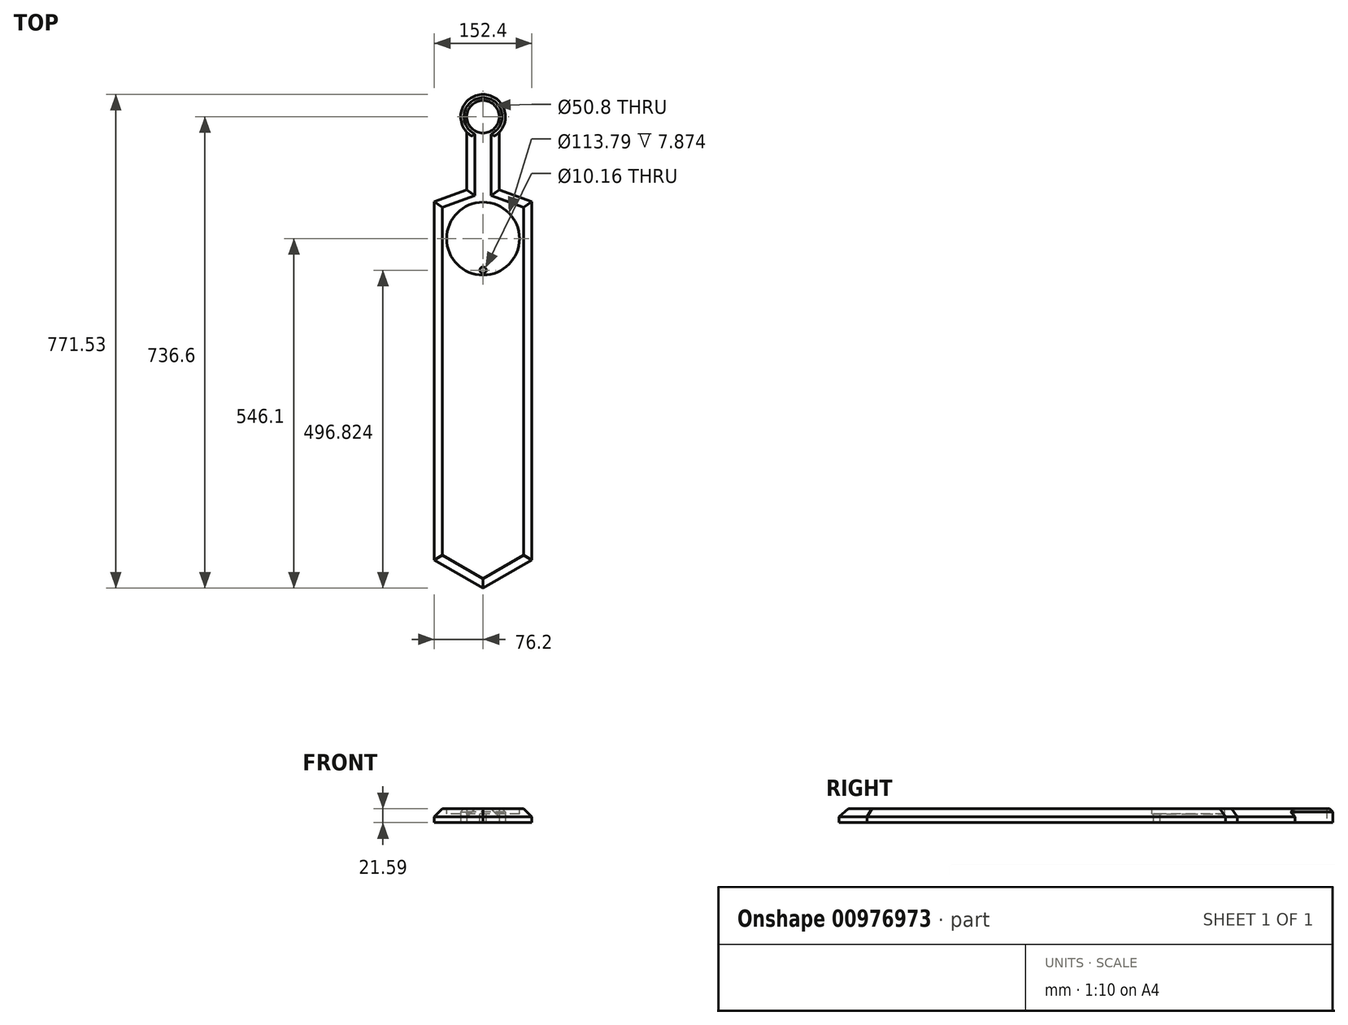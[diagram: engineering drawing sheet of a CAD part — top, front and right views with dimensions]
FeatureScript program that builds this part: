
annotation { "Feature Type Name" : "Feature", "Feature Type Description" : "" }
export const myFeature = defineFeature(function(context is Context, id is Id, definition is map)
    precondition{}
    {
        {
            var Q0;
            Q0=qCreatedBy(makeId("Top.planeOp"),FACE);
            var sketch = newSketch(context, id + "F0", { "sketchPlane" : qUnion([Q0])});
            skCircle(sketch, "E0", {"center": v(0, 0) * mm, "radius": 25.4 * mm});
            skLineSegment(sketch, "E1", {"start": v(-25.4, 0) * mm, "end": v(-25.4, -114.3) * mm});
            skLineSegment(sketch, "E2", {"start": v(-25.4, -114.3) * mm, "end": v(-76.2, -132.79) * mm});
            skLineSegment(sketch, "E3", {"start": v(-76.2, -132.79) * mm, "end": v(-76.2, -692.6) * mm});
            skLineSegment(sketch, "E4", {"start": v(0, -736.6) * mm, "end": v(-76.2, -692.6) * mm});
            skLineSegment(sketch, "E5", {"start": v(0, 0) * mm, "end": v(0, -736.6) * mm, "construction": true});
            skLineSegment(sketch, "E6.MirrorCS", {"start": v(76.2, -132.79) * mm, "end": v(76.2, -692.6) * mm});
            skLineSegment(sketch, "E7.MirrorCS", {"start": v(0, -736.6) * mm, "end": v(76.2, -692.6) * mm});
            skLineSegment(sketch, "E8.MirrorCS", {"start": v(25.4, 0) * mm, "end": v(25.4, -114.3) * mm});
            skLineSegment(sketch, "E9.MirrorCS", {"start": v(25.4, -114.3) * mm, "end": v(76.2, -132.79) * mm});
            skCircle(sketch, "E10", {"center": v(0, 0) * mm, "radius": 34.93 * mm});
            skSolve(sketch);
        }
        {
            var Q0;
            {var subQ0=sQuery(id+"F0.wireOp",EDGE,"E1");Q0=makeQuery(id+"F0.imprint","IMPRINT",FACE,{"disambiguationData":[TD([[makeQuery(id+"F0.imprint","IMPRINT",EDGE,{"derivedFrom":subQ0}),1.0]])]});}
            var Q1;
            {var subQ0=sQuery(id+"F0.wireOp",EDGE,"E0");var subQ1=makeQuery(id+"F0.imprint","INTERSECT",VERTEX,{"derivedFrom":[sQuery(id+"F0.wireOp",EDGE,"E1"),subQ0]});Q1=makeQuery(id+"F0.imprint","IMPRINT",FACE,{"disambiguationData":[TD([[makeQuery(id+"F0.imprint","IMPRINT",EDGE,{"disambiguationData":[TD([[subQ1,-1.0]])],"derivedFrom":subQ0}),-1.0]])]});}
            var Q2;
            {var subQ0=sQuery(id+"F0.wireOp",EDGE,"E0");var subQ1=sQuery(id+"F0.wireOp",EDGE,"E1");var subQ2=makeQuery(id+"F0.imprint","INTERSECT",VERTEX,{"derivedFrom":[subQ1,subQ0]});Q2=makeQuery(id+"F0.imprint","IMPRINT",FACE,{"disambiguationData":[TD([[makeQuery(id+"F0.imprint","IMPRINT",EDGE,{"disambiguationData":[TD([[subQ2,-1.0]])],"derivedFrom":subQ1}),-1.0]])]});}
            var Q3;
            {var subQ0=sQuery(id+"F0.wireOp",EDGE,"E2");Q3=makeQuery(id+"F0.imprint","IMPRINT",FACE,{"disambiguationData":[TD([[makeQuery(id+"F0.imprint","IMPRINT",EDGE,{"derivedFrom":subQ0}),1.0]])]});}
            extrude(context, id + "F1", {"entities" : qUnion([Q0, Q1, Q2, Q3]), "depth" : 21.59 * mm, "offsetDistance" : 25.4 * mm});
        }
        {
            var Q0;
            Q0=makeQuery(id+"F1.opExtrude","CAP_FACE",FACE,{"disambiguationData":[OSD([sQuery(id+"F0.wireOp",EDGE,"E1"),sQuery(id+"F0.wireOp",EDGE,"E2"),sQuery(id+"F0.wireOp",EDGE,"E3"),sQuery(id+"F0.wireOp",EDGE,"E4"),sQuery(id+"F0.wireOp",EDGE,"E6.MirrorCS"),sQuery(id+"F0.wireOp",EDGE,"E7.MirrorCS"),sQuery(id+"F0.wireOp",EDGE,"E8.MirrorCS"),sQuery(id+"F0.wireOp",EDGE,"E9.MirrorCS"),sQuery(id+"F0.wireOp",EDGE,"E10")])],"isStart":false});
            var sketch = newSketch(context, id + "F2", { "sketchPlane" : qUnion([Q0])});
            skCircle(sketch, "E11", {"center": v(0, -190.5) * mm, "radius": 56.9 * mm});
            skSolve(sketch);
        }
        {
            var Q0;
            Q0=makeQuery(id+"F2.imprint","IMPRINT",FACE,{"disambiguationData":[TD([[makeQuery(id+"F2.imprint","IMPRINT",EDGE,{"derivedFrom":sQuery(id+"F2.wireOp",EDGE,"E11")}),1.0]])]});
            extrude(context, id + "F3", {"entities" : qUnion([Q0]), "operationType" : NewBodyOperationType.REMOVE, "oppositeDirection" : true, "depth" : 7.87 * mm, "offsetDistance" : 25.4 * mm});
        }
        {
            var Q0;
            Q0=makeQuery(id+"F3.boolean.opBoolean","COPY",FACE,{"derivedFrom":makeQuery(id+"F3.opExtrude","CAP_FACE",FACE,{"disambiguationData":[OSD([sQuery(id+"F2.wireOp",EDGE,"E11")])],"isStart":false})});
            var sketch = newSketch(context, id + "F4", { "sketchPlane" : qUnion([Q0])});
            skCircle(sketch, "E12", {"center": v(0, -239.78) * mm, "radius": 5.08 * mm});
            skSolve(sketch);
        }
        {
            var Q0;
            Q0=makeQuery(id+"F4.imprint","IMPRINT",FACE,{"disambiguationData":[TD([[makeQuery(id+"F4.imprint","IMPRINT",EDGE,{"derivedFrom":sQuery(id+"F4.wireOp",EDGE,"E12")}),1.0]])]});
            extrude(context, id + "F5", {"entities" : qUnion([Q0]), "operationType" : NewBodyOperationType.REMOVE, "endBound" : BoundingType.THROUGH_ALL, "oppositeDirection" : true, "depth" : 25.4 * mm, "offsetDistance" : 25.4 * mm});
        }
        {
            var Q0;
            Q0=makeQuery(id+"F1.opExtrude","CAP_EDGE",EDGE,{"disambiguationData":[OSD([sQuery(id+"F0.wireOp",EDGE,"E3")])],"isStart":false});
            var Q1;
            Q1=makeQuery(id+"F1.opExtrude","CAP_EDGE",EDGE,{"disambiguationData":[OSD([sQuery(id+"F0.wireOp",EDGE,"E4")])],"isStart":false});
            var Q2;
            Q2=makeQuery(id+"F1.opExtrude","CAP_EDGE",EDGE,{"disambiguationData":[OSD([sQuery(id+"F0.wireOp",EDGE,"E7.MirrorCS")])],"isStart":false});
            var Q3;
            Q3=makeQuery(id+"F1.opExtrude","CAP_EDGE",EDGE,{"disambiguationData":[OSD([sQuery(id+"F0.wireOp",EDGE,"E6.MirrorCS")])],"isStart":false});
            var Q4;
            Q4=makeQuery(id+"F1.opExtrude","CAP_EDGE",EDGE,{"disambiguationData":[OSD([sQuery(id+"F0.wireOp",EDGE,"E9.MirrorCS")])],"isStart":false});
            var Q5;
            Q5=makeQuery(id+"F1.opExtrude","CAP_EDGE",EDGE,{"disambiguationData":[OSD([sQuery(id+"F0.wireOp",EDGE,"E2")])],"isStart":false});
            var Q6;
            Q6=makeQuery(id+"F1.opExtrude","CAP_EDGE",EDGE,{"disambiguationData":[OSD([sQuery(id+"F0.wireOp",EDGE,"E8.MirrorCS")])],"isStart":false});
            var Q7;
            Q7=makeQuery(id+"F1.opExtrude","CAP_EDGE",EDGE,{"disambiguationData":[OSD([sQuery(id+"F0.wireOp",EDGE,"E1")])],"isStart":false});
            chamfer(context, id + "F6", {"entities" : qUnion([Q0, Q1, Q2, Q3, Q4, Q5, Q6, Q7]), "width" : 12.7 * mm, "tangentPropagation" : true});
        }
        {
            var Q0;
            Q0=makeQuery(id+"F1.opExtrude","CAP_FACE",FACE,{"disambiguationData":[OSD([sQuery(id+"F0.wireOp",EDGE,"E1"),sQuery(id+"F0.wireOp",EDGE,"E2"),sQuery(id+"F0.wireOp",EDGE,"E3"),sQuery(id+"F0.wireOp",EDGE,"E4"),sQuery(id+"F0.wireOp",EDGE,"E6.MirrorCS"),sQuery(id+"F0.wireOp",EDGE,"E7.MirrorCS"),sQuery(id+"F0.wireOp",EDGE,"E8.MirrorCS"),sQuery(id+"F0.wireOp",EDGE,"E9.MirrorCS"),sQuery(id+"F0.wireOp",EDGE,"E10")])],"isStart":false});
            var sketch = newSketch(context, id + "F7", { "sketchPlane" : qUnion([Q0])});
            skCircle(sketch, "E13", {"center": v(0, 0) * mm, "radius": 3.18 * mm});
            skSolve(sketch);
        }
        {
            var Q0;
            Q0=makeQuery(id+"F7.imprint","IMPRINT",FACE,{"disambiguationData":[TD([[makeQuery(id+"F7.imprint","IMPRINT",EDGE,{"derivedFrom":sQuery(id+"F7.wireOp",EDGE,"E13")}),1.0]])]});
            extrude(context, id + "F8", {"entities" : qUnion([Q0]), "operationType" : NewBodyOperationType.REMOVE, "endBound" : BoundingType.THROUGH_ALL, "oppositeDirection" : true, "depth" : 25.4 * mm, "offsetDistance" : 25.4 * mm});
        }
        {
            var Q0;
            Q0=makeQuery(id+"F1.opExtrude","CAP_EDGE",EDGE,{"disambiguationData":[OSD([sQuery(id+"F0.wireOp",EDGE,"E10")])],"isStart":false});
            chamfer(context, id + "F9", {"entities" : qUnion([Q0]), "width" : 5.08 * mm, "tangentPropagation" : true});
        }
    });
